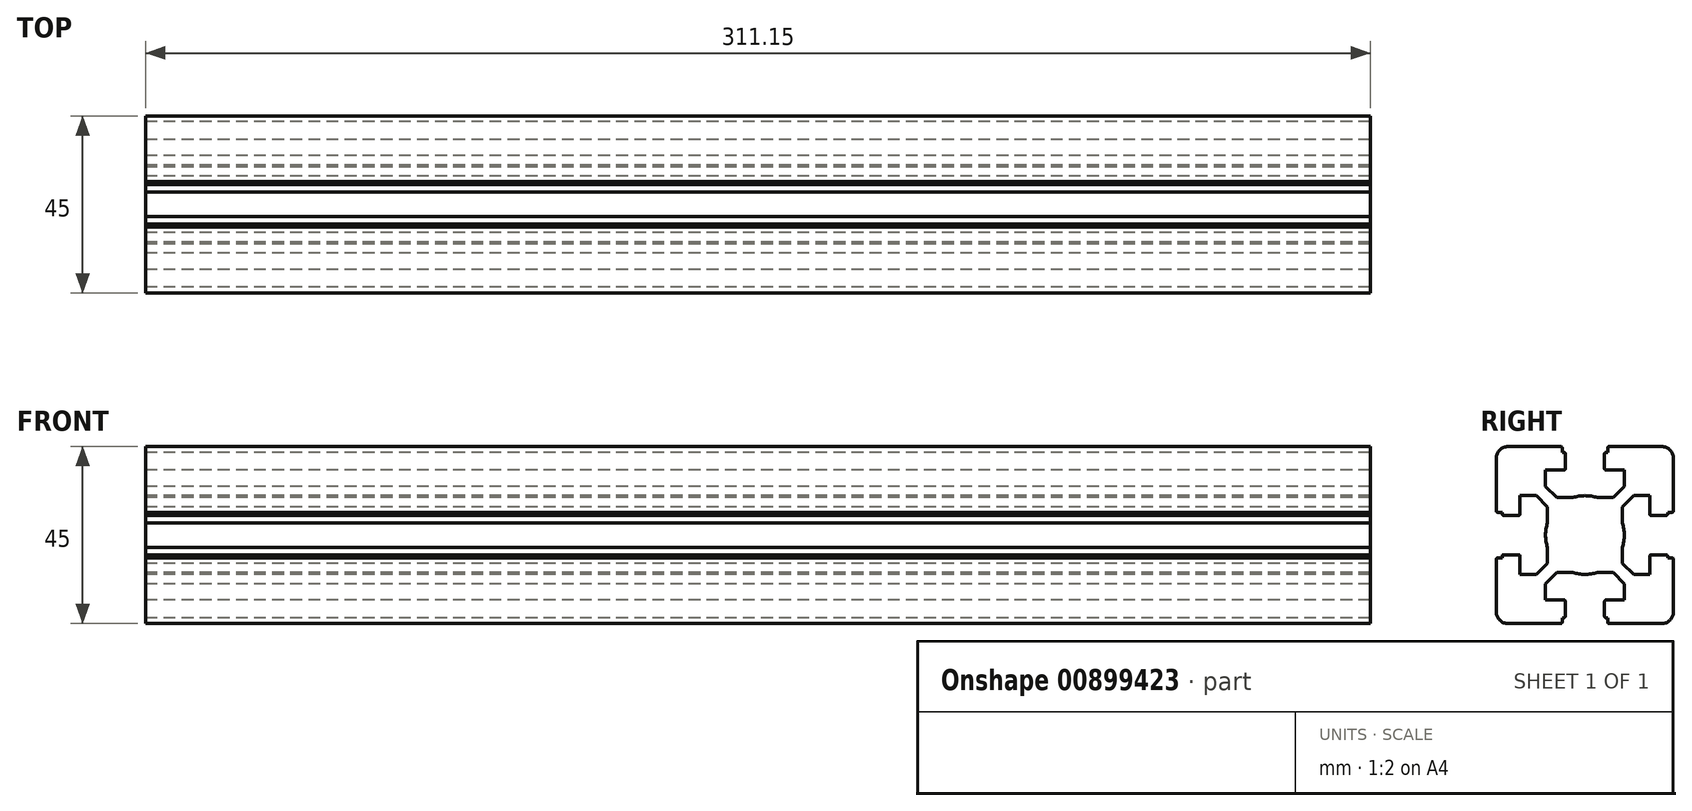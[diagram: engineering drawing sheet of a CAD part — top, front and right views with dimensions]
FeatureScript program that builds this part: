
annotation { "Feature Type Name" : "Feature", "Feature Type Description" : "" }
export const myFeature = defineFeature(function(context is Context, id is Id, definition is map)
    precondition{}
    {
        {
            var Q0;
            Q0=qCreatedBy(makeId("Right.planeOp"),FACE);
            var sketch = newSketch(context, id + "F0", { "sketchPlane" : qUnion([Q0])});
            skLineSegment(sketch, "E0", {"start": v(-20.09, -10.29) * mm, "end": v(-21.29, -10.29) * mm});
            skArc(sketch, "E1", {"start": v(-21.29, -10.29) * mm, "mid": v(-21.5, -10.38) * mm, "end": v(-21.59, -10.59) * mm});
            skLineSegment(sketch, "E2", {"start": v(-21.59, -10.59) * mm, "end": v(-21.59, -23.99) * mm});
            skArc(sketch, "E3", {"start": v(-21.59, -23.99) * mm, "mid": v(-20.7, -26.11) * mm, "end": v(-18.59, -26.99) * mm});
            skLineSegment(sketch, "E4", {"start": v(-18.59, -26.99) * mm, "end": v(-5.19, -26.99) * mm});
            skArc(sketch, "E5", {"start": v(-5.19, -26.99) * mm, "mid": v(-4.98, -26.9) * mm, "end": v(-4.89, -26.69) * mm});
            skLineSegment(sketch, "E6", {"start": v(-4.89, -26.69) * mm, "end": v(-4.89, -25.49) * mm});
            skLineSegment(sketch, "E7", {"start": v(-4.89, -25.49) * mm, "end": v(-4.39, -25.49) * mm});
            skArc(sketch, "E8", {"start": v(-4.39, -25.49) * mm, "mid": v(-4.18, -25.4) * mm, "end": v(-4.09, -25.19) * mm});
            skLineSegment(sketch, "E9", {"start": v(-4.09, -25.19) * mm, "end": v(-4.09, -21.29) * mm});
            skArc(sketch, "E10", {"start": v(-4.09, -21.29) * mm, "mid": v(-4.18, -21.08) * mm, "end": v(-4.39, -20.99) * mm});
            skLineSegment(sketch, "E11", {"start": v(-4.39, -20.99) * mm, "end": v(-9.14, -20.99) * mm});
            skLineSegment(sketch, "E12", {"start": v(-9.14, -20.99) * mm, "end": v(-9.14, -16.88) * mm});
            skLineSegment(sketch, "E13", {"start": v(-9.14, -16.88) * mm, "end": v(-6.25, -13.99) * mm});
            skLineSegment(sketch, "E14", {"start": v(-6.25, -13.99) * mm, "end": v(-2.21, -13.99) * mm});
            skArc(sketch, "E15", {"start": v(-2.21, -13.99) * mm, "mid": v(0.91, -14.49) * mm, "end": v(4.03, -13.99) * mm});
            skLineSegment(sketch, "E16", {"start": v(-20.09, -10.29) * mm, "end": v(-20.09, -9.79) * mm});
            skArc(sketch, "E17", {"start": v(-20.09, -9.79) * mm, "mid": v(-20, -9.58) * mm, "end": v(-19.79, -9.49) * mm});
            skLineSegment(sketch, "E18", {"start": v(-19.79, -9.49) * mm, "end": v(-15.89, -9.49) * mm});
            skArc(sketch, "E19", {"start": v(-15.89, -9.49) * mm, "mid": v(-15.68, -9.58) * mm, "end": v(-15.59, -9.79) * mm});
            skLineSegment(sketch, "E20", {"start": v(-15.59, -9.79) * mm, "end": v(-15.59, -14.54) * mm});
            skLineSegment(sketch, "E21", {"start": v(-15.59, -14.54) * mm, "end": v(-11.48, -14.54) * mm});
            skLineSegment(sketch, "E22", {"start": v(-11.48, -14.54) * mm, "end": v(-8.59, -11.65) * mm});
            skLineSegment(sketch, "E23", {"start": v(-8.59, -11.65) * mm, "end": v(-8.59, -7.61) * mm});
            skLineSegment(sketch, "E24", {"start": v(29.82, -4.49) * mm, "end": v(-31.05, -4.49) * mm});
            skLineSegment(sketch, "E25.MirrorCS", {"start": v(6.71, -25.49) * mm, "end": v(6.21, -25.49) * mm});
            skArc(sketch, "E26.MirrorCS", {"start": v(7.01, -26.99) * mm, "mid": v(6.8, -26.9) * mm, "end": v(6.71, -26.69) * mm});
            skLineSegment(sketch, "E27.MirrorCS", {"start": v(10.41, -11.65) * mm, "end": v(10.41, -7.61) * mm});
            skArc(sketch, "E28.MirrorCS", {"start": v(6.21, -25.49) * mm, "mid": v(6, -25.4) * mm, "end": v(5.91, -25.19) * mm});
            skLineSegment(sketch, "E29.MirrorCS", {"start": v(6.71, -26.69) * mm, "end": v(6.71, -25.49) * mm});
            skArc(sketch, "E30.MirrorCS", {"start": v(5.91, -21.29) * mm, "mid": v(6, -21.08) * mm, "end": v(6.21, -20.99) * mm});
            skLineSegment(sketch, "E31.MirrorCS", {"start": v(10.96, -16.88) * mm, "end": v(8.07, -13.99) * mm});
            skLineSegment(sketch, "E32.MirrorCS", {"start": v(13.3, -14.54) * mm, "end": v(10.41, -11.65) * mm});
            skLineSegment(sketch, "E33.MirrorCS", {"start": v(17.41, -14.54) * mm, "end": v(13.3, -14.54) * mm});
            skLineSegment(sketch, "E34.MirrorCS", {"start": v(17.41, -9.79) * mm, "end": v(17.41, -14.54) * mm});
            skLineSegment(sketch, "E35.MirrorCS", {"start": v(6.21, -20.99) * mm, "end": v(10.96, -20.99) * mm});
            skLineSegment(sketch, "E36.MirrorCS", {"start": v(8.07, -13.99) * mm, "end": v(4.03, -13.99) * mm});
            skArc(sketch, "E37.MirrorCS", {"start": v(4.03, -13.99) * mm, "mid": v(0.91, -14.49) * mm, "end": v(-2.21, -13.99) * mm});
            skLineSegment(sketch, "E38.MirrorCS", {"start": v(10.96, -20.99) * mm, "end": v(10.96, -16.88) * mm});
            skLineSegment(sketch, "E39.MirrorCS", {"start": v(5.91, -25.19) * mm, "end": v(5.91, -21.29) * mm});
            skArc(sketch, "E40.MirrorCS", {"start": v(23.41, -23.99) * mm, "mid": v(22.53, -26.11) * mm, "end": v(20.41, -26.99) * mm});
            skLineSegment(sketch, "E41.MirrorCS", {"start": v(20.41, -26.99) * mm, "end": v(7.01, -26.99) * mm});
            skLineSegment(sketch, "E42.MirrorCS", {"start": v(23.41, -10.59) * mm, "end": v(23.41, -23.99) * mm});
            skArc(sketch, "E43.MirrorCS", {"start": v(17.71, -9.49) * mm, "mid": v(17.5, -9.58) * mm, "end": v(17.41, -9.79) * mm});
            skArc(sketch, "E44.MirrorCS", {"start": v(23.11, -10.29) * mm, "mid": v(23.32, -10.38) * mm, "end": v(23.41, -10.59) * mm});
            skLineSegment(sketch, "E45.MirrorCS", {"start": v(21.91, -10.29) * mm, "end": v(21.91, -9.79) * mm});
            skLineSegment(sketch, "E46.MirrorCS", {"start": v(21.91, -10.29) * mm, "end": v(23.11, -10.29) * mm});
            skArc(sketch, "E47.MirrorCS", {"start": v(21.91, -9.79) * mm, "mid": v(21.82, -9.58) * mm, "end": v(21.61, -9.49) * mm});
            skLineSegment(sketch, "E48.MirrorCS", {"start": v(21.61, -9.49) * mm, "end": v(17.71, -9.49) * mm});
            skLineSegment(sketch, "E49.MirrorCS", {"start": v(6.71, 16.51) * mm, "end": v(6.21, 16.51) * mm});
            skArc(sketch, "E50.MirrorCS", {"start": v(-4.39, 16.51) * mm, "mid": v(-4.18, 16.42) * mm, "end": v(-4.09, 16.21) * mm});
            skLineSegment(sketch, "E51.MirrorCS", {"start": v(-4.89, 16.51) * mm, "end": v(-4.39, 16.51) * mm});
            skArc(sketch, "E52.MirrorCS", {"start": v(5.91, 12.31) * mm, "mid": v(6, 12.1) * mm, "end": v(6.21, 12.01) * mm});
            skLineSegment(sketch, "E53.MirrorCS", {"start": v(6.71, 17.71) * mm, "end": v(6.71, 16.51) * mm});
            skLineSegment(sketch, "E54.MirrorCS", {"start": v(-4.89, 17.71) * mm, "end": v(-4.89, 16.51) * mm});
            skArc(sketch, "E55.MirrorCS", {"start": v(-5.19, 18.01) * mm, "mid": v(-4.98, 17.92) * mm, "end": v(-4.89, 17.71) * mm});
            skArc(sketch, "E56.MirrorCS", {"start": v(-4.09, 12.31) * mm, "mid": v(-4.18, 12.1) * mm, "end": v(-4.39, 12.01) * mm});
            skArc(sketch, "E57.MirrorCS", {"start": v(7.01, 18.01) * mm, "mid": v(6.8, 17.92) * mm, "end": v(6.71, 17.71) * mm});
            skArc(sketch, "E58.MirrorCS", {"start": v(6.21, 16.51) * mm, "mid": v(6, 16.42) * mm, "end": v(5.91, 16.21) * mm});
            skArc(sketch, "E59.MirrorCS", {"start": v(23.11, 1.31) * mm, "mid": v(23.32, 1.4) * mm, "end": v(23.41, 1.61) * mm});
            skLineSegment(sketch, "E60.MirrorCS", {"start": v(21.91, 1.31) * mm, "end": v(21.91, 0.81) * mm});
            skArc(sketch, "E61.MirrorCS", {"start": v(-15.89, 0.51) * mm, "mid": v(-15.68, 0.6) * mm, "end": v(-15.59, 0.81) * mm});
            skArc(sketch, "E62.MirrorCS", {"start": v(-21.29, 1.31) * mm, "mid": v(-21.5, 1.4) * mm, "end": v(-21.59, 1.61) * mm});
            skArc(sketch, "E63.MirrorCS", {"start": v(17.71, 0.51) * mm, "mid": v(17.5, 0.6) * mm, "end": v(17.41, 0.81) * mm});
            skArc(sketch, "E64.MirrorCS", {"start": v(21.91, 0.81) * mm, "mid": v(21.82, 0.6) * mm, "end": v(21.61, 0.51) * mm});
            skLineSegment(sketch, "E65.MirrorCS", {"start": v(21.91, 1.31) * mm, "end": v(23.11, 1.31) * mm});
            skArc(sketch, "E66.MirrorCS", {"start": v(14.31, 5.31) * mm, "mid": v(14.1, 5.4) * mm, "end": v(14.01, 5.61) * mm});
            skArc(sketch, "E67.MirrorCS", {"start": v(-20.09, 0.81) * mm, "mid": v(-20, 0.6) * mm, "end": v(-19.79, 0.51) * mm});
            skLineSegment(sketch, "E68.MirrorCS", {"start": v(-20.09, 1.31) * mm, "end": v(-21.29, 1.31) * mm});
            skLineSegment(sketch, "E69.MirrorCS", {"start": v(-20.09, 1.31) * mm, "end": v(-20.09, 0.81) * mm});
            skLineSegment(sketch, "E70.MirrorCS", {"start": v(8.07, 5.01) * mm, "end": v(4.03, 5.01) * mm});
            skLineSegment(sketch, "E71.MirrorCS", {"start": v(-4.09, 16.21) * mm, "end": v(-4.09, 12.31) * mm});
            skLineSegment(sketch, "E72.MirrorCS", {"start": v(-9.14, 12.01) * mm, "end": v(-9.14, 7.9) * mm});
            skLineSegment(sketch, "E73.MirrorCS", {"start": v(-15.59, 5.56) * mm, "end": v(-11.48, 5.56) * mm});
            skLineSegment(sketch, "E74.MirrorCS", {"start": v(-4.39, 12.01) * mm, "end": v(-9.14, 12.01) * mm});
            skLineSegment(sketch, "E75.MirrorCS", {"start": v(-9.14, 7.9) * mm, "end": v(-6.25, 5.01) * mm});
            skLineSegment(sketch, "E76.MirrorCS", {"start": v(10.96, 12.01) * mm, "end": v(10.96, 7.9) * mm});
            skArc(sketch, "E77.MirrorCS", {"start": v(-21.59, 15.01) * mm, "mid": v(-20.7, 17.13) * mm, "end": v(-18.59, 18.01) * mm});
            skLineSegment(sketch, "E78.MirrorCS", {"start": v(23.41, 1.61) * mm, "end": v(23.41, 15.01) * mm});
            skLineSegment(sketch, "E79.MirrorCS", {"start": v(13.3, 5.56) * mm, "end": v(10.41, 2.67) * mm});
            skLineSegment(sketch, "E80.MirrorCS", {"start": v(-8.59, 2.67) * mm, "end": v(-8.59, -1.37) * mm});
            skLineSegment(sketch, "E81.MirrorCS", {"start": v(-15.59, 0.81) * mm, "end": v(-15.59, 5.56) * mm});
            skLineSegment(sketch, "E82.MirrorCS", {"start": v(10.41, 2.67) * mm, "end": v(10.41, -1.37) * mm});
            skLineSegment(sketch, "E83.MirrorCS", {"start": v(-18.59, 18.01) * mm, "end": v(-5.19, 18.01) * mm});
            skLineSegment(sketch, "E84.MirrorCS", {"start": v(10.96, 7.9) * mm, "end": v(8.07, 5.01) * mm});
            skLineSegment(sketch, "E85.MirrorCS", {"start": v(17.41, 5.56) * mm, "end": v(13.3, 5.56) * mm});
            skArc(sketch, "E86.MirrorCS", {"start": v(23.41, 15.01) * mm, "mid": v(22.53, 17.13) * mm, "end": v(20.41, 18.01) * mm});
            skLineSegment(sketch, "E87.MirrorCS", {"start": v(5.91, 16.21) * mm, "end": v(5.91, 12.31) * mm});
            skLineSegment(sketch, "E88.MirrorCS", {"start": v(17.41, 0.81) * mm, "end": v(17.41, 5.56) * mm});
            skLineSegment(sketch, "E89.MirrorCS", {"start": v(-11.48, 5.56) * mm, "end": v(-8.59, 2.67) * mm});
            skLineSegment(sketch, "E90.MirrorCS", {"start": v(-6.25, 5.01) * mm, "end": v(-2.21, 5.01) * mm});
            skLineSegment(sketch, "E91.MirrorCS", {"start": v(-21.59, 1.61) * mm, "end": v(-21.59, 15.01) * mm});
            skArc(sketch, "E92.MirrorCS", {"start": v(4.03, 5.01) * mm, "mid": v(0.91, 5.51) * mm, "end": v(-2.21, 5.01) * mm});
            skLineSegment(sketch, "E93.MirrorCS", {"start": v(6.21, 12.01) * mm, "end": v(10.96, 12.01) * mm});
            skArc(sketch, "E94.MirrorCS", {"start": v(-2.21, 5.01) * mm, "mid": v(0.91, 5.51) * mm, "end": v(4.03, 5.01) * mm});
            skLineSegment(sketch, "E95.MirrorCS", {"start": v(20.41, 18.01) * mm, "end": v(7.01, 18.01) * mm});
            skLineSegment(sketch, "E96.MirrorCS", {"start": v(-19.79, 0.51) * mm, "end": v(-15.89, 0.51) * mm});
            skLineSegment(sketch, "E97.MirrorCS", {"start": v(21.61, 0.51) * mm, "end": v(17.71, 0.51) * mm});
            skLineSegment(sketch, "E98.MirrorCS", {"start": v(0.91, -27.65) * mm, "end": v(0.91, 19.82) * mm});
            skArc(sketch, "E99", {"start": v(-8.59, -1.37) * mm, "mid": v(-9.09, -4.49) * mm, "end": v(-8.59, -7.61) * mm});
            skArc(sketch, "E100", {"start": v(10.41, -7.61) * mm, "mid": v(10.91, -4.49) * mm, "end": v(10.41, -1.37) * mm});
            skSolve(sketch);
        }
        {
            var Q0;
            Q0=qSketchRegion(id+"F0",true);
            extrude(context, id + "F1", {"entities" : qUnion([Q0]), "depth" : 311.15 * mm, "offsetDistance" : 25.4 * mm});
        }
    });
